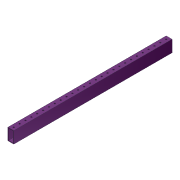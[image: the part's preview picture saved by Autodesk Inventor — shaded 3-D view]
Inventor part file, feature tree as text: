
AUTODESK INVENTOR PART (.ipt)
format: ipt  version: 2012 (Build 160160000, 160)  size: 136,192 bytes
history: native  units: in
note: dims shown in document units (in); Inventor stores cm internally (conversion verified against a paired STEP export)
features: extrude x2, sketch x2, pattern_linear x1
ambient origin geometry x8: Origin, YZ Plane, XZ Plane, XY Plane, X Axis, Y Axis, Z Axis, Center Point
bodies: Solid1 (feature_tree)
feature tree (5):
  extrude  "Extrusion1"  Depth=1.0in
  extrude  "Extrusion2"  Depth=0.125in
  pattern_linear  "Rectangular Pattern1"  Spacing1=0.125in  [1 undecoded]
  sketch  "Sketch1"  dims[d0=2.0in d1=1.0in]
  sketch  "Sketch2"  dims[d2=0.125in d3=0.125in d4=0.125in d5=0.125in d6=27.0in d7=0.0in d8=0.25in d9=0.5in d10=0.5in d11=1.0in d12=0.0in d13=10.6299in d15=1.0in]
note: 1 required parameter value undecoded (feature->parameter linkage not recoverable at this tier; creation-order binding heuristic only, values carry confidence <= 0.55)
